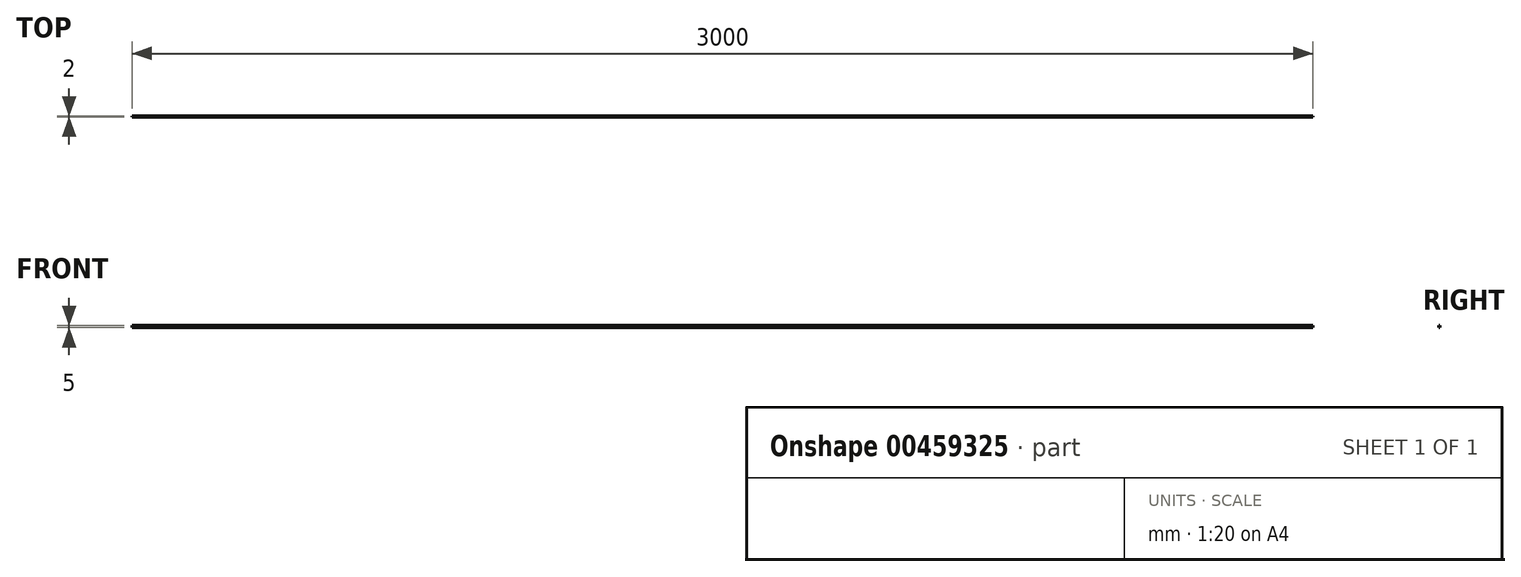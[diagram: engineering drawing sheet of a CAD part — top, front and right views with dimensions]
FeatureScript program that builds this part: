
annotation { "Feature Type Name" : "Feature", "Feature Type Description" : "" }
export const myFeature = defineFeature(function(context is Context, id is Id, definition is map)
    precondition{}
    {
        {
            var Q0;
            Q0=qCreatedBy(makeId("Front.planeOp"),FACE);
            var sketch = newSketch(context, id + "F0", { "sketchPlane" : qUnion([Q0])});
            skLineSegment(sketch, "E0.bottom", {"start": v(0, 0) * mm, "end": v(3000, 0) * mm});
            skLineSegment(sketch, "E0.top", {"start": v(0, 5) * mm, "end": v(3000, 5) * mm});
            skLineSegment(sketch, "E0.left", {"start": v(0, 0) * mm, "end": v(0, 5) * mm});
            skLineSegment(sketch, "E0.right", {"start": v(3000, 0) * mm, "end": v(3000, 5) * mm});
            skSolve(sketch);
        }
        {
            var Q0;
            Q0 = qSketchRegion(id + "F0", true);
            extrude(context, id + "F1", {"entities" : qUnion([Q0]), "depth" : 2 * mm});
        }
    });
